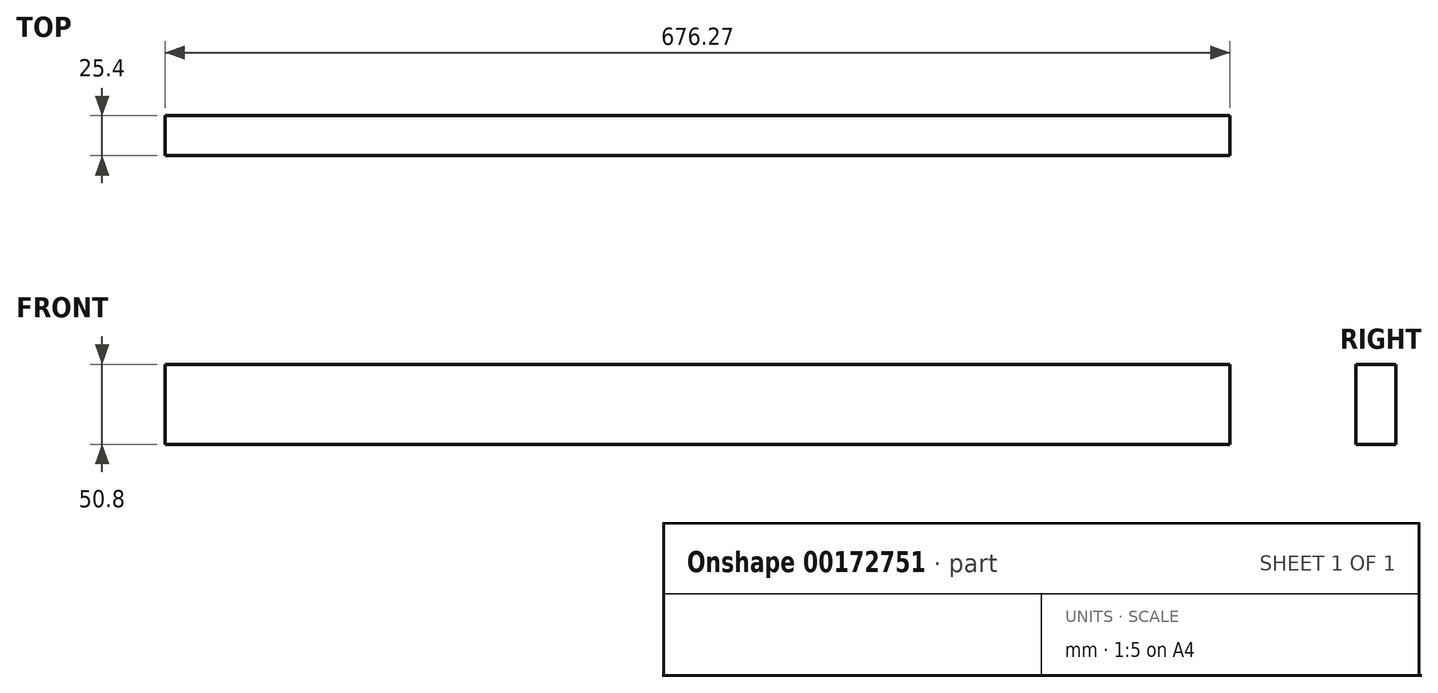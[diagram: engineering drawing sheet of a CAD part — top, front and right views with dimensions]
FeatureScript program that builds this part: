
annotation { "Feature Type Name" : "Feature", "Feature Type Description" : "" }
export const myFeature = defineFeature(function(context is Context, id is Id, definition is map)
    precondition{}
    {
        {
            var Q0;
            Q0=qCreatedBy(makeId("Front.planeOp"),FACE);
            var sketch = newSketch(context, id + "F0", { "sketchPlane" : qUnion([Q0])});
            skLineSegment(sketch, "E0.bottom", {"start": v(-349.36, -8.06) * mm, "end": v(326.91, -8.06) * mm});
            skLineSegment(sketch, "E0.top", {"start": v(-349.36, -58.86) * mm, "end": v(326.91, -58.86) * mm});
            skLineSegment(sketch, "E0.left", {"start": v(-349.36, -8.06) * mm, "end": v(-349.36, -58.86) * mm});
            skLineSegment(sketch, "E0.right", {"start": v(326.91, -8.06) * mm, "end": v(326.91, -58.86) * mm});
            skSolve(sketch);
        }
        {
            var Q0;
            Q0 = qSketchRegion(id + "F0", true);
            extrude(context, id + "F1", {"entities" : qUnion([Q0]), "depth" : 25.4 * mm});
        }
    });
